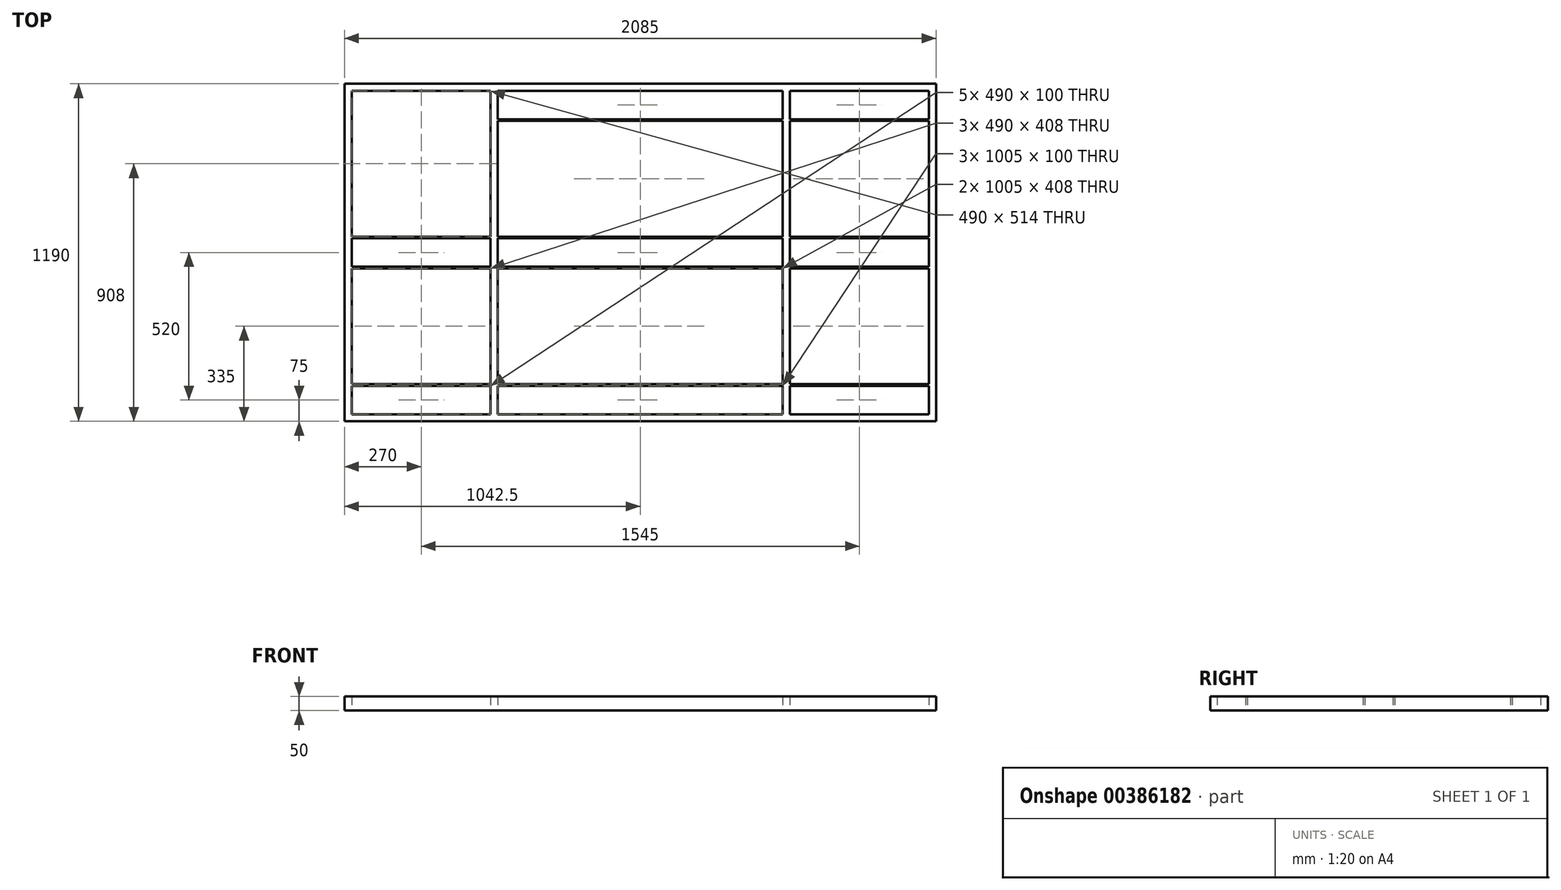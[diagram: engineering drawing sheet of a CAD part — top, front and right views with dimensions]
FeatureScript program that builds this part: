
annotation { "Feature Type Name" : "Feature", "Feature Type Description" : "" }
export const myFeature = defineFeature(function(context is Context, id is Id, definition is map)
    precondition{}
    {
        {
            var Q0;
            Q0=qCreatedBy(makeId("Top.planeOp"),FACE);
            var sketch = newSketch(context, id + "F0", { "sketchPlane" : qUnion([Q0])});
            skLineSegment(sketch, "E0.bottom", {"start": v(0, 0) * mm, "end": v(540, 0) * mm});
            skLineSegment(sketch, "E0.top", {"start": v(0, 1190) * mm, "end": v(540, 1190) * mm});
            skLineSegment(sketch, "E0.left", {"start": v(0, 0) * mm, "end": v(0, 1190) * mm});
            skLineSegment(sketch, "E0.right", {"start": v(540, 0) * mm, "end": v(540, 1190) * mm});
            skLineSegment(sketch, "E1.0", {"start": v(25, 1165) * mm, "end": v(515, 1165) * mm});
            skLineSegment(sketch, "E1.1", {"start": v(25, 25) * mm, "end": v(25, 1165) * mm});
            skLineSegment(sketch, "E1.2", {"start": v(25, 25) * mm, "end": v(515, 25) * mm});
            skLineSegment(sketch, "E1.3", {"start": v(515, 25) * mm, "end": v(515, 1165) * mm});
            skLineSegment(sketch, "E2", {"start": v(759.37, 595) * mm, "end": v(-360.82, 595) * mm, "construction": true});
            skLineSegment(sketch, "E3.bottom", {"start": v(25, 125) * mm, "end": v(515, 125) * mm});
            skLineSegment(sketch, "E3.top", {"start": v(25, 131) * mm, "end": v(515, 131) * mm});
            skLineSegment(sketch, "E3.left", {"start": v(25, 125) * mm, "end": v(25, 131) * mm});
            skLineSegment(sketch, "E3.right", {"start": v(515, 125) * mm, "end": v(515, 131) * mm});
            skLineSegment(sketch, "E4.bottom", {"start": v(25, 545) * mm, "end": v(515, 545) * mm});
            skLineSegment(sketch, "E4.top", {"start": v(25, 539) * mm, "end": v(515, 539) * mm});
            skLineSegment(sketch, "E4.left", {"start": v(25, 545) * mm, "end": v(25, 539) * mm});
            skLineSegment(sketch, "E4.right", {"start": v(515, 545) * mm, "end": v(515, 539) * mm});
            skLineSegment(sketch, "E5.MirrorCS", {"start": v(25, 645) * mm, "end": v(515, 645) * mm});
            skLineSegment(sketch, "E6.MirrorCS", {"start": v(25, 651) * mm, "end": v(515, 651) * mm});
            skLineSegment(sketch, "E7.MirrorCS", {"start": v(25, 1065) * mm, "end": v(25, 1059) * mm});
            skLineSegment(sketch, "E8.MirrorCS", {"start": v(515, 1065) * mm, "end": v(515, 1059) * mm});
            skLineSegment(sketch, "E9.MirrorCS", {"start": v(25, 1059) * mm, "end": v(515, 1059) * mm});
            skLineSegment(sketch, "E10.MirrorCS", {"start": v(25, 1065) * mm, "end": v(515, 1065) * mm});
            skLineSegment(sketch, "E11.1.0.0", {"start": v(540, 1165) * mm, "end": v(1030, 1165) * mm});
            skLineSegment(sketch, "E11.1.0.1", {"start": v(540, 1065) * mm, "end": v(1030, 1065) * mm});
            skLineSegment(sketch, "E11.1.0.2", {"start": v(515, 1190) * mm, "end": v(1055, 1190) * mm});
            skLineSegment(sketch, "E11.1.0.3", {"start": v(540, 545) * mm, "end": v(1030, 545) * mm});
            skLineSegment(sketch, "E11.1.0.4", {"start": v(540, 131) * mm, "end": v(1030, 131) * mm});
            skLineSegment(sketch, "E11.1.0.5", {"start": v(540, 651) * mm, "end": v(1030, 651) * mm});
            skLineSegment(sketch, "E11.1.0.6", {"start": v(540, 1059) * mm, "end": v(1030, 1059) * mm});
            skLineSegment(sketch, "E11.1.0.7", {"start": v(515, 0) * mm, "end": v(1055, 0) * mm});
            skLineSegment(sketch, "E11.1.0.8", {"start": v(1030, 25) * mm, "end": v(1030, 1165) * mm, "construction": true});
            skLineSegment(sketch, "E11.1.0.9", {"start": v(540, 539) * mm, "end": v(1030, 539) * mm});
            skLineSegment(sketch, "E11.1.0.10", {"start": v(540, 125) * mm, "end": v(1030, 125) * mm});
            skLineSegment(sketch, "E11.1.0.11", {"start": v(1274.37, 595) * mm, "end": v(154.18, 595) * mm, "construction": true});
            skLineSegment(sketch, "E11.1.0.12", {"start": v(540, 25) * mm, "end": v(1030, 25) * mm});
            skLineSegment(sketch, "E11.1.0.13", {"start": v(1055, 0) * mm, "end": v(1055, 1190) * mm, "construction": true});
            skLineSegment(sketch, "E11.1.0.14", {"start": v(540, 645) * mm, "end": v(1030, 645) * mm});
            skLineSegment(sketch, "E11.1.0.15", {"start": v(1030, 1065) * mm, "end": v(1030, 1059) * mm});
            skLineSegment(sketch, "E11.1.0.16", {"start": v(1030, 545) * mm, "end": v(1030, 539) * mm});
            skLineSegment(sketch, "E11.1.0.17", {"start": v(1030, 125) * mm, "end": v(1030, 131) * mm});
            skLineSegment(sketch, "E11.2.0.0", {"start": v(1055, 1165) * mm, "end": v(1545, 1165) * mm});
            skLineSegment(sketch, "E11.2.0.1", {"start": v(1055, 1065) * mm, "end": v(1545, 1065) * mm});
            skLineSegment(sketch, "E11.2.0.2", {"start": v(1030, 1190) * mm, "end": v(1570, 1190) * mm});
            skLineSegment(sketch, "E11.2.0.3", {"start": v(1055, 545) * mm, "end": v(1545, 545) * mm});
            skLineSegment(sketch, "E11.2.0.4", {"start": v(1055, 131) * mm, "end": v(1545, 131) * mm});
            skLineSegment(sketch, "E11.2.0.5", {"start": v(1055, 651) * mm, "end": v(1545, 651) * mm});
            skLineSegment(sketch, "E11.2.0.6", {"start": v(1055, 1059) * mm, "end": v(1545, 1059) * mm});
            skLineSegment(sketch, "E11.2.0.7", {"start": v(1030, 0) * mm, "end": v(1570, 0) * mm});
            skLineSegment(sketch, "E11.2.0.8", {"start": v(1545, 25) * mm, "end": v(1545, 1165) * mm});
            skLineSegment(sketch, "E11.2.0.9", {"start": v(1055, 539) * mm, "end": v(1545, 539) * mm});
            skLineSegment(sketch, "E11.2.0.10", {"start": v(1055, 125) * mm, "end": v(1545, 125) * mm});
            skLineSegment(sketch, "E11.2.0.11", {"start": v(1789.37, 595) * mm, "end": v(669.18, 595) * mm, "construction": true});
            skLineSegment(sketch, "E11.2.0.12", {"start": v(1055, 25) * mm, "end": v(1545, 25) * mm});
            skLineSegment(sketch, "E11.2.0.13", {"start": v(1570, 0) * mm, "end": v(1570, 1190) * mm});
            skLineSegment(sketch, "E11.2.0.14", {"start": v(1055, 645) * mm, "end": v(1545, 645) * mm});
            skLineSegment(sketch, "E11.2.0.15", {"start": v(1545, 1065) * mm, "end": v(1545, 1059) * mm});
            skLineSegment(sketch, "E11.2.0.16", {"start": v(1545, 545) * mm, "end": v(1545, 539) * mm});
            skLineSegment(sketch, "E11.2.0.17", {"start": v(1545, 125) * mm, "end": v(1545, 131) * mm});
            skLineSegment(sketch, "E11.direction1", {"start": v(0, 0) * mm, "end": v(515, 0) * mm, "construction": true});
            skLineSegment(sketch, "E12.0.3.0", {"start": v(1570, 1165) * mm, "end": v(2060, 1165) * mm});
            skLineSegment(sketch, "E12.3.3.0", {"start": v(1570, 1065) * mm, "end": v(2060, 1065) * mm});
            skLineSegment(sketch, "E12.6.3.0", {"start": v(1545, 1190) * mm, "end": v(2085, 1190) * mm});
            skLineSegment(sketch, "E12.9.3.0", {"start": v(1570, 545) * mm, "end": v(2060, 545) * mm});
            skLineSegment(sketch, "E12.12.3.0", {"start": v(1570, 131) * mm, "end": v(2060, 131) * mm});
            skLineSegment(sketch, "E12.15.3.0", {"start": v(1570, 651) * mm, "end": v(2060, 651) * mm});
            skLineSegment(sketch, "E12.18.3.0", {"start": v(1570, 1059) * mm, "end": v(2060, 1059) * mm});
            skLineSegment(sketch, "E12.21.3.0", {"start": v(1545, 0) * mm, "end": v(2085, 0) * mm});
            skLineSegment(sketch, "E12.24.3.0", {"start": v(2060, 25) * mm, "end": v(2060, 1165) * mm});
            skLineSegment(sketch, "E12.27.3.0", {"start": v(1570, 539) * mm, "end": v(2060, 539) * mm});
            skLineSegment(sketch, "E12.30.3.0", {"start": v(1570, 125) * mm, "end": v(2060, 125) * mm});
            skLineSegment(sketch, "E12.33.3.0", {"start": v(2304.37, 595) * mm, "end": v(1184.18, 595) * mm, "construction": true});
            skLineSegment(sketch, "E12.36.3.0", {"start": v(1570, 25) * mm, "end": v(2060, 25) * mm});
            skLineSegment(sketch, "E12.39.3.0", {"start": v(2085, 0) * mm, "end": v(2085, 1190) * mm});
            skLineSegment(sketch, "E12.42.3.0", {"start": v(1570, 645) * mm, "end": v(2060, 645) * mm});
            skLineSegment(sketch, "E12.45.3.0", {"start": v(2060, 1065) * mm, "end": v(2060, 1059) * mm});
            skLineSegment(sketch, "E12.48.3.0", {"start": v(2060, 545) * mm, "end": v(2060, 539) * mm});
            skLineSegment(sketch, "E12.51.3.0", {"start": v(2060, 125) * mm, "end": v(2060, 131) * mm});
            skLineSegment(sketch, "E13.bottom", {"start": v(1030, 539) * mm, "end": v(1055, 539) * mm});
            skLineSegment(sketch, "E13.top", {"start": v(1030, 545) * mm, "end": v(1055, 545) * mm});
            skLineSegment(sketch, "E13.left", {"start": v(1030, 539) * mm, "end": v(1030, 545) * mm});
            skLineSegment(sketch, "E13.right", {"start": v(1055, 539) * mm, "end": v(1055, 545) * mm});
            skLineSegment(sketch, "E14.bottom", {"start": v(1030, 125) * mm, "end": v(1055, 125) * mm});
            skLineSegment(sketch, "E14.top", {"start": v(1030, 131) * mm, "end": v(1055, 131) * mm});
            skLineSegment(sketch, "E14.right", {"start": v(1055, 125) * mm, "end": v(1055, 131) * mm});
            skLineSegment(sketch, "E15.bottom", {"start": v(1055, 1065) * mm, "end": v(1030, 1065) * mm});
            skLineSegment(sketch, "E15.top", {"start": v(1055, 1059) * mm, "end": v(1030, 1059) * mm});
            skLineSegment(sketch, "E15.left", {"start": v(1055, 1065) * mm, "end": v(1055, 1059) * mm});
            skLineSegment(sketch, "E16.bottom", {"start": v(1055, 645) * mm, "end": v(1030, 645) * mm});
            skLineSegment(sketch, "E16.top", {"start": v(1055, 651) * mm, "end": v(1030, 651) * mm});
            skLineSegment(sketch, "E16.left", {"start": v(1055, 645) * mm, "end": v(1055, 651) * mm});
            skLineSegment(sketch, "E16.right", {"start": v(1030, 645) * mm, "end": v(1030, 651) * mm});
            skLineSegment(sketch, "E17", {"start": v(1030, 1165) * mm, "end": v(1055, 1165) * mm});
            skLineSegment(sketch, "E18", {"start": v(1030, 25) * mm, "end": v(1055, 25) * mm});
            skSolve(sketch);
        }
        {
            var Q0;
            Q0=qSketchRegion(id+"F0",true);
            var Q1;
            Q1=makeQuery(id+"F0.imprint","IMPRINT",FACE,{"disambiguationData":[TD([[makeQuery(id+"F0.imprint","IMPRINT",EDGE,{"derivedFrom":sQuery(id+"F0.wireOp",EDGE,"E4.bottom")}),-1.0]])]});
            var Q2;
            Q2=makeQuery(id+"F0.imprint","IMPRINT",FACE,{"disambiguationData":[TD([[makeQuery(id+"F0.imprint","IMPRINT",EDGE,{"derivedFrom":sQuery(id+"F0.wireOp",EDGE,"baab227e-6a5d-40b9-91ee-7446e1ab67f20.MirrorCS")}),1.0]])]});
            var Q3;
            Q3=makeQuery(id+"F0.imprint","IMPRINT",FACE,{"disambiguationData":[TD([[makeQuery(id+"F0.imprint","IMPRINT",EDGE,{"derivedFrom":sQuery(id+"F0.wireOp",EDGE,"E3.bottom")}),1.0]])]});
            var Q4;
            Q4=makeQuery(id+"F0.imprint","IMPRINT",FACE,{"disambiguationData":[TD([[makeQuery(id+"F0.imprint","IMPRINT",EDGE,{"derivedFrom":sQuery(id+"F0.wireOp",EDGE,"TbBb99Yr-0gyQ-v6ej-gQRB-Bgt5jI2MECaT.bottom")}),-1.0]])]});
            var Q5;
            Q5=makeQuery(id+"F0.imprint","IMPRINT",FACE,{"disambiguationData":[TD([[makeQuery(id+"F0.imprint","IMPRINT",EDGE,{"derivedFrom":sQuery(id+"F0.wireOp",EDGE,"NzViuoU3-R4T5-xjC5-rI0y-QMhb7gm5c65x.bottom")}),-1.0]])]});
            var Q6;
            Q6=makeQuery(id+"F0.imprint","IMPRINT",FACE,{"disambiguationData":[TD([[makeQuery(id+"F0.imprint","IMPRINT",EDGE,{"derivedFrom":sQuery(id+"F0.wireOp",EDGE,"baab227e-6a5d-40b9-91ee-7446e1ab67f23.MirrorCS")}),-1.0]])]});
            var Q7;
            Q7=makeQuery(id+"F0.imprint","IMPRINT",FACE,{"disambiguationData":[TD([[makeQuery(id+"F0.imprint","IMPRINT",EDGE,{"derivedFrom":sQuery(id+"F0.wireOp",EDGE,"baab227e-6a5d-40b9-91ee-7446e1ab67f22.MirrorCS")}),-1.0]])]});
            var Q8;
            Q8=makeQuery(id+"F0.imprint","IMPRINT",FACE,{"disambiguationData":[TD([[makeQuery(id+"F0.imprint","IMPRINT",EDGE,{"derivedFrom":sQuery(id+"F0.wireOp",EDGE,"baab227e-6a5d-40b9-91ee-7446e1ab67f21.MirrorCS")}),1.0]])]});
            var Q9;
            {var subQ0=sQuery(id+"F0.wireOp",EDGE,"E5.MirrorCS");Q9=makeQuery(id+"F0.imprint","IMPRINT",FACE,{"disambiguationData":[TD([[makeQuery(id+"F0.imprint","IMPRINT",EDGE,{"derivedFrom":subQ0}),1.0]])]});}
            var Q10;
            Q10=makeQuery(id+"F0.imprint","IMPRINT",FACE,{"disambiguationData":[TD([[makeQuery(id+"F0.imprint","IMPRINT",EDGE,{"derivedFrom":sQuery(id+"F0.wireOp",EDGE,"E7.MirrorCS")}),1.0]])]});
            var Q11;
            {var subQ0=sQuery(id+"F0.wireOp",EDGE,"E11.1.0.5");Q11=makeQuery(id+"F0.imprint","IMPRINT",FACE,{"disambiguationData":[TD([[makeQuery(id+"F0.imprint","IMPRINT",EDGE,{"derivedFrom":subQ0}),-1.0]])]});}
            var Q12;
            {var subQ0=sQuery(id+"F0.wireOp",EDGE,"E11.2.0.5");Q12=makeQuery(id+"F0.imprint","IMPRINT",FACE,{"disambiguationData":[TD([[makeQuery(id+"F0.imprint","IMPRINT",EDGE,{"derivedFrom":subQ0}),-1.0]])]});}
            var Q13;
            {var subQ0=sQuery(id+"F0.wireOp",EDGE,"E11.2.0.3");Q13=makeQuery(id+"F0.imprint","IMPRINT",FACE,{"disambiguationData":[TD([[makeQuery(id+"F0.imprint","IMPRINT",EDGE,{"derivedFrom":subQ0}),-1.0]])]});}
            var Q14;
            {var subQ0=sQuery(id+"F0.wireOp",EDGE,"E11.1.0.3");Q14=makeQuery(id+"F0.imprint","IMPRINT",FACE,{"disambiguationData":[TD([[makeQuery(id+"F0.imprint","IMPRINT",EDGE,{"derivedFrom":subQ0}),-1.0]])]});}
            var Q15;
            {var subQ0=sQuery(id+"F0.wireOp",EDGE,"E12.9.3.0");Q15=makeQuery(id+"F0.imprint","IMPRINT",FACE,{"disambiguationData":[TD([[makeQuery(id+"F0.imprint","IMPRINT",EDGE,{"derivedFrom":subQ0}),-1.0]])]});}
            var Q16;
            {var subQ0=sQuery(id+"F0.wireOp",EDGE,"E12.15.3.0");Q16=makeQuery(id+"F0.imprint","IMPRINT",FACE,{"disambiguationData":[TD([[makeQuery(id+"F0.imprint","IMPRINT",EDGE,{"derivedFrom":subQ0}),-1.0]])]});}
            var Q17;
            {var subQ0=sQuery(id+"F0.wireOp",EDGE,"E12.3.3.0");Q17=makeQuery(id+"F0.imprint","IMPRINT",FACE,{"disambiguationData":[TD([[makeQuery(id+"F0.imprint","IMPRINT",EDGE,{"derivedFrom":subQ0}),-1.0]])]});}
            var Q18;
            {var subQ0=sQuery(id+"F0.wireOp",EDGE,"E11.2.0.1");Q18=makeQuery(id+"F0.imprint","IMPRINT",FACE,{"disambiguationData":[TD([[makeQuery(id+"F0.imprint","IMPRINT",EDGE,{"derivedFrom":subQ0}),-1.0]])]});}
            var Q19;
            {var subQ0=sQuery(id+"F0.wireOp",EDGE,"E11.1.0.1");Q19=makeQuery(id+"F0.imprint","IMPRINT",FACE,{"disambiguationData":[TD([[makeQuery(id+"F0.imprint","IMPRINT",EDGE,{"derivedFrom":subQ0}),-1.0]])]});}
            var Q20;
            {var subQ0=sQuery(id+"F0.wireOp",EDGE,"E12.12.3.0");Q20=makeQuery(id+"F0.imprint","IMPRINT",FACE,{"disambiguationData":[TD([[makeQuery(id+"F0.imprint","IMPRINT",EDGE,{"derivedFrom":subQ0}),-1.0]])]});}
            var Q21;
            {var subQ0=sQuery(id+"F0.wireOp",EDGE,"E11.1.0.4");Q21=makeQuery(id+"F0.imprint","IMPRINT",FACE,{"disambiguationData":[TD([[makeQuery(id+"F0.imprint","IMPRINT",EDGE,{"derivedFrom":subQ0}),-1.0]])]});}
            var Q22;
            {var subQ0=sQuery(id+"F0.wireOp",EDGE,"E11.2.0.4");Q22=makeQuery(id+"F0.imprint","IMPRINT",FACE,{"disambiguationData":[TD([[makeQuery(id+"F0.imprint","IMPRINT",EDGE,{"derivedFrom":subQ0}),-1.0]])]});}
            var Q23;
            Q23=makeQuery(id+"F0.imprint","IMPRINT",FACE,{"disambiguationData":[TD([[makeQuery(id+"F0.imprint","IMPRINT",EDGE,{"derivedFrom":sQuery(id+"F0.wireOp",EDGE,"E14.bottom")}),1.0]])]});
            var Q24;
            Q24=makeQuery(id+"F0.imprint","IMPRINT",FACE,{"disambiguationData":[TD([[makeQuery(id+"F0.imprint","IMPRINT",EDGE,{"derivedFrom":sQuery(id+"F0.wireOp",EDGE,"E13.bottom")}),1.0]])]});
            var Q25;
            Q25=makeQuery(id+"F0.imprint","IMPRINT",FACE,{"disambiguationData":[TD([[makeQuery(id+"F0.imprint","IMPRINT",EDGE,{"derivedFrom":sQuery(id+"F0.wireOp",EDGE,"E15.bottom")}),1.0]])]});
            var Q26;
            Q26=makeQuery(id+"F0.imprint","IMPRINT",FACE,{"disambiguationData":[TD([[makeQuery(id+"F0.imprint","IMPRINT",EDGE,{"derivedFrom":sQuery(id+"F0.wireOp",EDGE,"E16.bottom")}),-1.0]])]});
            extrude(context, id + "F1", {"entities" : qUnion([Q0, Q1, Q2, Q3, Q4, Q5, Q6, Q7, Q8, Q9, Q10, Q11, Q12, Q13, Q14, Q15, Q16, Q17, Q18, Q19, Q20, Q21, Q22, Q23, Q24, Q25, Q26]), "depth" : 50 * mm});
        }
        {
            var Q0;
            Q0=makeQuery(id+"F1.opExtrude","SWEPT_FACE",FACE,{"disambiguationData":[OSD([sQuery(id+"F0.wireOp",EDGE,"E3.top")])]});
            var sketch = newSketch(context, id + "F2", { "sketchPlane" : qUnion([Q0])});
            skLineSegment(sketch, "E19", {"start": v(-265, -37.36) * mm, "end": v(-265, 103.2) * mm, "construction": true});
            skPoint(sketch, "E19.startSnap0", {"position": v(-265, 25) * mm});
            skCircle(sketch, "E20", {"center": v(-265, 25) * mm, "radius": 9.5 * mm});
            skLineSegment(sketch, "E21", {"start": v(-25, 25) * mm, "end": v(-265, 25) * mm, "construction": true});
            skLineSegment(sketch, "E22", {"start": v(-515, 25) * mm, "end": v(-265, 25) * mm, "construction": true});
            skCircle(sketch, "E23", {"center": v(-145, 25) * mm, "radius": 9.5 * mm});
            skCircle(sketch, "E24", {"center": v(-390, 25) * mm, "radius": 9.5 * mm});
            skLineSegment(sketch, "E25", {"start": v(-527.5, -35.14) * mm, "end": v(-527.5, 158.1) * mm, "construction": true});
            skCircle(sketch, "E26.MirrorC", {"center": v(-790, 25) * mm, "radius": 9.5 * mm});
            skCircle(sketch, "E27.MirrorC", {"center": v(-910, 25) * mm, "radius": 9.5 * mm});
            skCircle(sketch, "E28.MirrorC", {"center": v(-665, 25) * mm, "radius": 9.5 * mm});
            skLineSegment(sketch, "E29", {"start": v(-1042.5, -68.6) * mm, "end": v(-1042.5, 150.41) * mm, "construction": true});
            skCircle(sketch, "E30.MirrorC", {"center": v(-1820, 25) * mm, "radius": 9.5 * mm});
            skCircle(sketch, "E31.MirrorC", {"center": v(-1295, 25) * mm, "radius": 9.5 * mm});
            skCircle(sketch, "E32.MirrorC", {"center": v(-1695, 25) * mm, "radius": 9.5 * mm});
            skCircle(sketch, "E33.MirrorC", {"center": v(-1175, 25) * mm, "radius": 9.5 * mm});
            skCircle(sketch, "E34.MirrorC", {"center": v(-1940, 25) * mm, "radius": 9.5 * mm});
            skCircle(sketch, "E35.MirrorC", {"center": v(-1420, 25) * mm, "radius": 9.5 * mm});
            skLineSegment(sketch, "E36", {"start": v(-910, 25) * mm, "end": v(-1175, 25) * mm, "construction": true});
            skCircle(sketch, "E37", {"center": v(-1042.5, 25) * mm, "radius": 9.5 * mm});
            skSolve(sketch);
        }
        {
            var Q0;
            Q0=sQuery(id+"F2.wireOp",EDGE,"E23");
            var Q1;
            Q1=sQuery(id+"F2.wireOp",EDGE,"E20");
            var Q2;
            Q2=sQuery(id+"F2.wireOp",EDGE,"E24");
            var Q3;
            Q3=sQuery(id+"F2.wireOp",EDGE,"E28.MirrorC");
            var Q4;
            Q4=sQuery(id+"F2.wireOp",EDGE,"E26.MirrorC");
            var Q5;
            Q5=sQuery(id+"F2.wireOp",EDGE,"E27.MirrorC");
            var Q6;
            Q6=sQuery(id+"F2.wireOp",EDGE,"E33.MirrorC");
            var Q7;
            Q7=sQuery(id+"F2.wireOp",EDGE,"E31.MirrorC");
            var Q8;
            Q8=sQuery(id+"F2.wireOp",EDGE,"E35.MirrorC");
            var Q9;
            Q9=sQuery(id+"F2.wireOp",EDGE,"E32.MirrorC");
            var Q10;
            Q10=sQuery(id+"F2.wireOp",EDGE,"E30.MirrorC");
            var Q11;
            Q11=sQuery(id+"F2.wireOp",EDGE,"E34.MirrorC");
            var Q12;
            Q12=sQuery(id+"F2.wireOp",EDGE,"E37");
            extrude(context, id + "F3", {"bodyType" : ToolBodyType.SURFACE, "surfaceEntities" : qUnion([Q0, Q1, Q2, Q3, Q4, Q5, Q6, Q7, Q8, Q9, Q10, Q11, Q12]), "endBound" : BoundingType.UP_TO_NEXT, "depth" : 25 * mm});
        }
        {
            var Q0;
            Q0=makeQuery(id+"F1.opExtrude","SWEPT_FACE",FACE,{"disambiguationData":[OSD([sQuery(id+"F0.wireOp",EDGE,"E6.MirrorCS")])]});
            var sketch = newSketch(context, id + "F4", { "sketchPlane" : qUnion([Q0])});
            skLineSegment(sketch, "E38", {"start": v(-515, 25) * mm, "end": v(-270, 25) * mm, "construction": true});
            skLineSegment(sketch, "E39", {"start": v(-270, 25) * mm, "end": v(-25, 25) * mm, "construction": true});
            skCircle(sketch, "E40", {"center": v(-392.5, 25) * mm, "radius": 9.5 * mm});
            skCircle(sketch, "E41", {"center": v(-270, 25) * mm, "radius": 9.5 * mm});
            skCircle(sketch, "E42", {"center": v(-147.5, 25) * mm, "radius": 9.5 * mm});
            skLineSegment(sketch, "E43", {"start": v(-540, 25) * mm, "end": v(-1030, 25) * mm, "construction": true});
            skLineSegment(sketch, "E44", {"start": v(-527.5, 96.55) * mm, "end": v(-527.5, -41.55) * mm, "construction": true});
            skLineSegment(sketch, "E45", {"start": v(-1042.5, -33.14) * mm, "end": v(-1042.5, 110.96) * mm, "construction": true});
            skCircle(sketch, "E46.MirrorC", {"center": v(-662.5, 25) * mm, "radius": 9.5 * mm});
            skCircle(sketch, "E47.MirrorC", {"center": v(-785, 25) * mm, "radius": 9.5 * mm});
            skCircle(sketch, "E48.MirrorC", {"center": v(-907.5, 25) * mm, "radius": 9.5 * mm});
            skCircle(sketch, "E49.MirrorC", {"center": v(-1177.5, 25) * mm, "radius": 9.5 * mm});
            skCircle(sketch, "E50.MirrorC", {"center": v(-1300, 25) * mm, "radius": 9.5 * mm});
            skCircle(sketch, "E51.MirrorC", {"center": v(-1422.5, 25) * mm, "radius": 9.5 * mm});
            skCircle(sketch, "E52.MirrorC", {"center": v(-1692.5, 25) * mm, "radius": 9.5 * mm});
            skCircle(sketch, "E53.MirrorC", {"center": v(-1815, 25) * mm, "radius": 9.5 * mm});
            skCircle(sketch, "E54.MirrorC", {"center": v(-1937.5, 25) * mm, "radius": 9.5 * mm});
            skLineSegment(sketch, "E55", {"start": v(-907.5, 25) * mm, "end": v(-1177.5, 25) * mm, "construction": true});
            skCircle(sketch, "E56", {"center": v(-1042.5, 25) * mm, "radius": 9.5 * mm});
            skSolve(sketch);
        }
        {
            var Q0;
            Q0=sQuery(id+"F4.wireOp",EDGE,"E42");
            var Q1;
            Q1=sQuery(id+"F4.wireOp",EDGE,"E41");
            var Q2;
            Q2=sQuery(id+"F4.wireOp",EDGE,"E40");
            var Q3;
            Q3=sQuery(id+"F4.wireOp",EDGE,"E46.MirrorC");
            var Q4;
            Q4=sQuery(id+"F4.wireOp",EDGE,"E47.MirrorC");
            var Q5;
            Q5=sQuery(id+"F4.wireOp",EDGE,"E48.MirrorC");
            var Q6;
            Q6=sQuery(id+"F4.wireOp",EDGE,"E49.MirrorC");
            var Q7;
            Q7=sQuery(id+"F4.wireOp",EDGE,"E50.MirrorC");
            var Q8;
            Q8=sQuery(id+"F4.wireOp",EDGE,"E51.MirrorC");
            var Q9;
            Q9=sQuery(id+"F4.wireOp",EDGE,"E52.MirrorC");
            var Q10;
            Q10=sQuery(id+"F4.wireOp",EDGE,"E53.MirrorC");
            var Q11;
            Q11=sQuery(id+"F4.wireOp",EDGE,"E54.MirrorC");
            var Q12;
            Q12=sQuery(id+"F4.wireOp",EDGE,"E56");
            extrude(context, id + "F5", {"bodyType" : ToolBodyType.SURFACE, "surfaceEntities" : qUnion([Q0, Q1, Q2, Q3, Q4, Q5, Q6, Q7, Q8, Q9, Q10, Q11, Q12]), "endBound" : BoundingType.UP_TO_NEXT, "depth" : 25 * mm});
        }
    });
